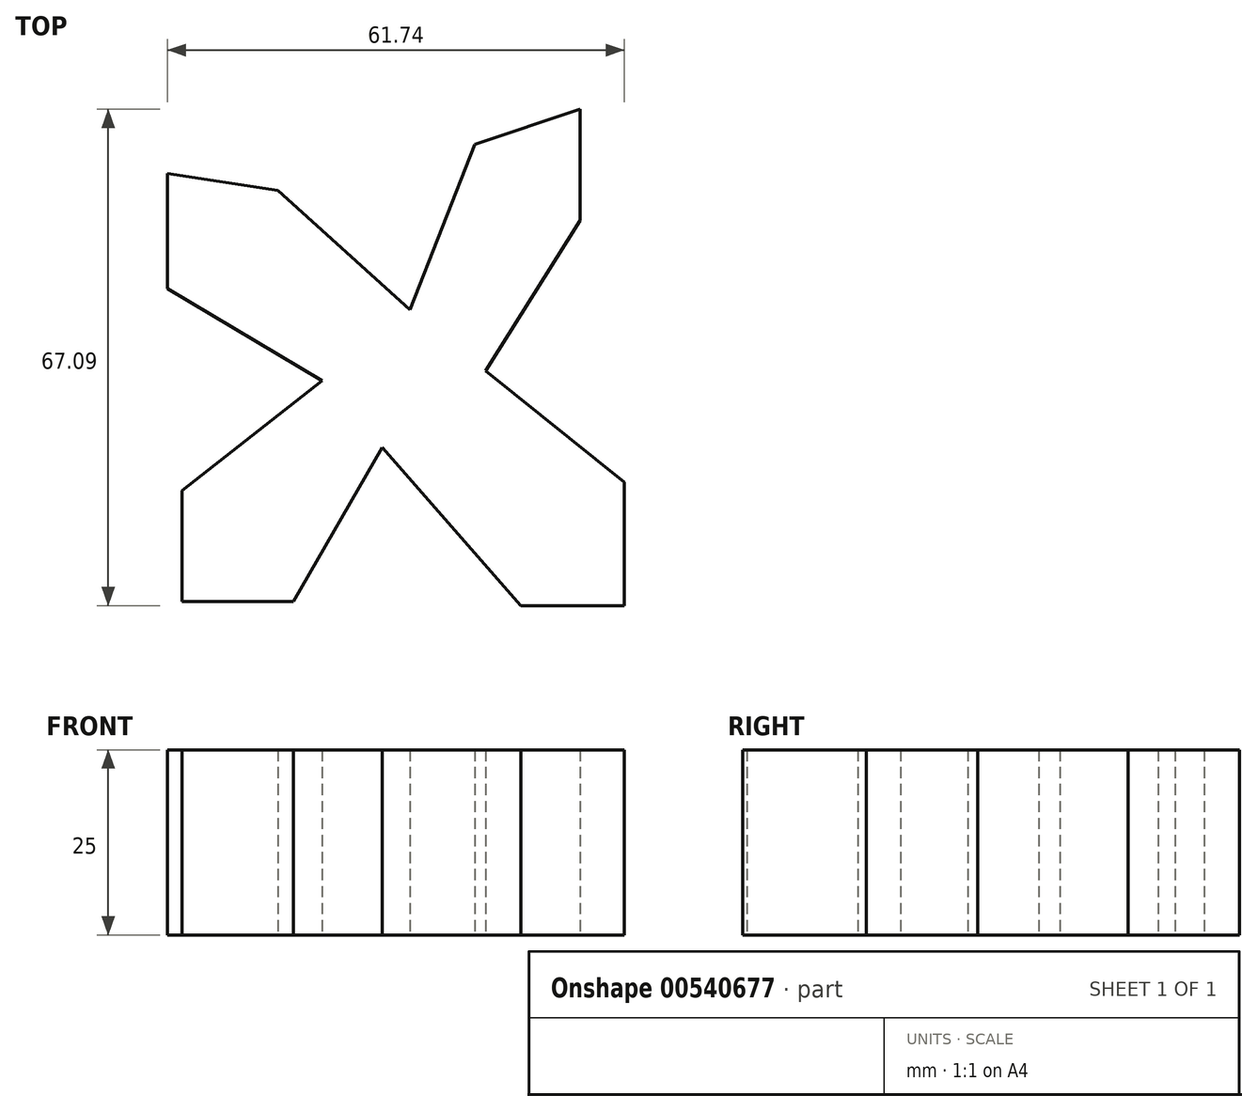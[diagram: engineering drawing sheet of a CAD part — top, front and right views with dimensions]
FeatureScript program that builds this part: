
annotation { "Feature Type Name" : "Feature", "Feature Type Description" : "" }
export const myFeature = defineFeature(function(context is Context, id is Id, definition is map)
    precondition{}
    {
        {
            var Q0;
            Q0=qCreatedBy(makeId("Top.planeOp"),FACE);
            var sketch = newSketch(context, id + "F0", { "sketchPlane" : qUnion([Q0])});
            skLineSegment(sketch, "E0", {"start": v(-59.74, -35.7) * mm, "end": v(-44.74, -35.7) * mm});
            skLineSegment(sketch, "E1", {"start": v(-44.74, -35.7) * mm, "end": v(-32.74, -14.92) * mm});
            skLineSegment(sketch, "E2", {"start": v(-59.74, -35.7) * mm, "end": v(-59.74, -20.7) * mm});
            skLineSegment(sketch, "E3", {"start": v(-59.74, -20.7) * mm, "end": v(-40.87, -5.88) * mm});
            skLineSegment(sketch, "E4", {"start": v(-40.87, -5.88) * mm, "end": v(-61.74, 6.6) * mm});
            skLineSegment(sketch, "E5", {"start": v(-61.74, 6.6) * mm, "end": v(-61.74, 22.14) * mm});
            skLineSegment(sketch, "E6", {"start": v(-61.74, 22.14) * mm, "end": v(-46.77, 19.84) * mm});
            skLineSegment(sketch, "E7", {"start": v(-46.77, 19.84) * mm, "end": v(-29, 3.72) * mm});
            skLineSegment(sketch, "E8", {"start": v(-29, 3.72) * mm, "end": v(-20.22, 26.06) * mm});
            skLineSegment(sketch, "E9", {"start": v(-20.22, 26.06) * mm, "end": v(-6, 30.8) * mm});
            skLineSegment(sketch, "E10", {"start": v(-6, 30.8) * mm, "end": v(-6, 15.8) * mm});
            skLineSegment(sketch, "E11", {"start": v(-6, 15.8) * mm, "end": v(-18.71, -4.54) * mm});
            skLineSegment(sketch, "E12", {"start": v(-18.71, -4.54) * mm, "end": v(0, -19.57) * mm});
            skLineSegment(sketch, "E13", {"start": v(0, -19.57) * mm, "end": v(0, -36.28) * mm});
            skLineSegment(sketch, "E14", {"start": v(0, -36.28) * mm, "end": v(-13.96, -36.28) * mm});
            skLineSegment(sketch, "E15", {"start": v(-13.96, -36.28) * mm, "end": v(-32.74, -14.92) * mm});
            skSolve(sketch);
        }
        {
            var Q0;
            Q0 = qSketchRegion(id + "F0", true);
            extrude(context, id + "F1", {"entities" : qUnion([Q0]), "depth" : 25 * mm, "offsetDistance" : 25 * mm});
        }
    });
